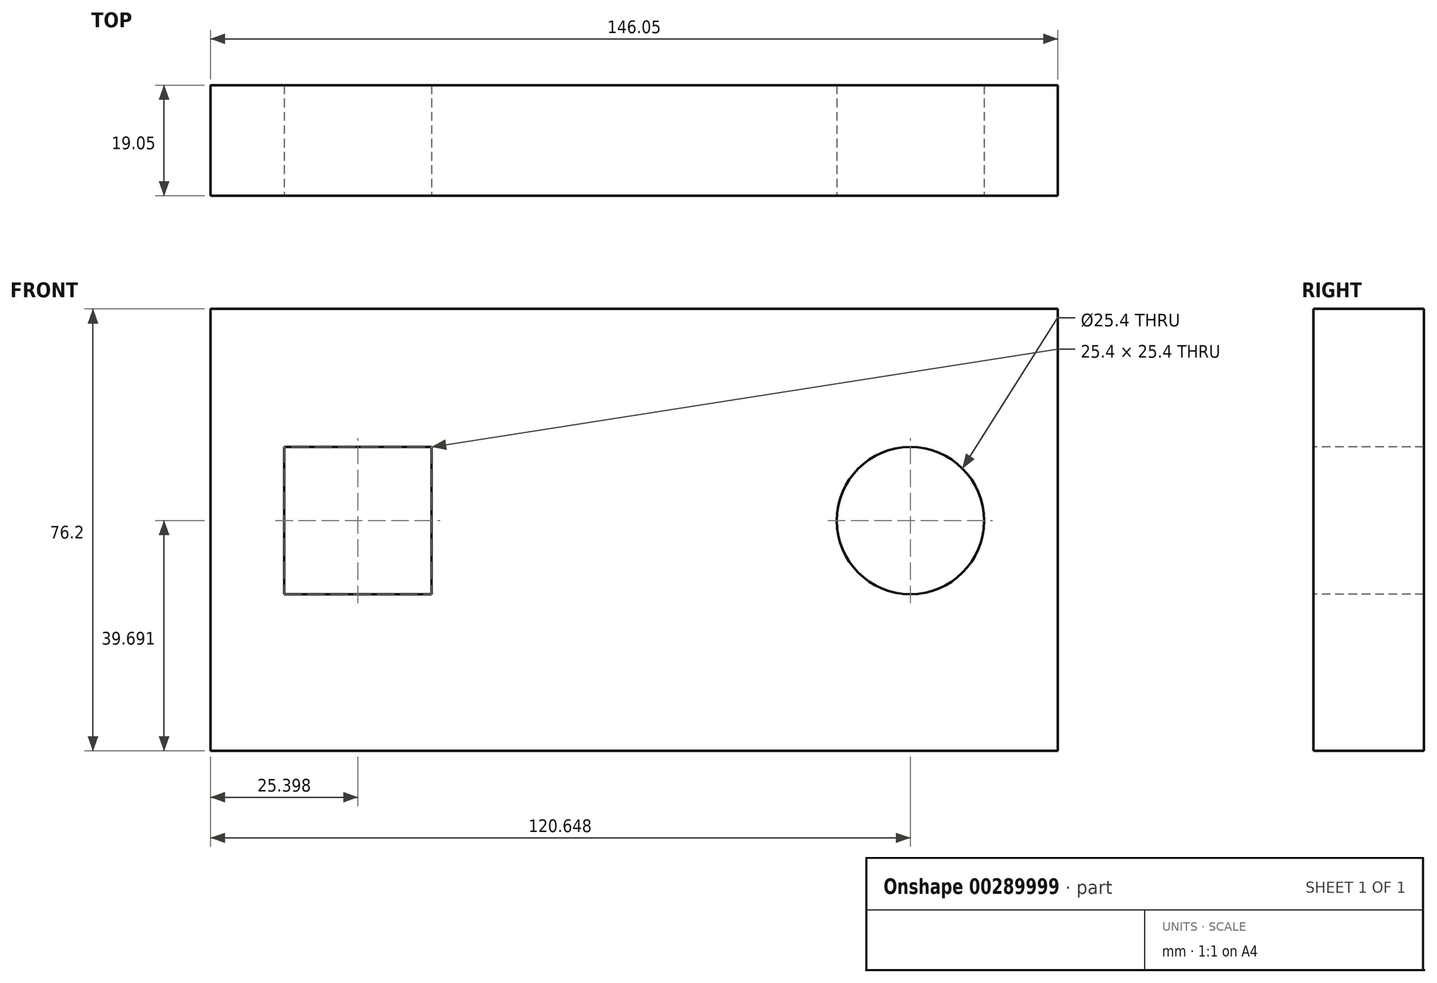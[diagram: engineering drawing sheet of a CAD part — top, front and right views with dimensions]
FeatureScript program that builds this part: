
annotation { "Feature Type Name" : "Feature", "Feature Type Description" : "" }
export const myFeature = defineFeature(function(context is Context, id is Id, definition is map)
    precondition{}
    {
        {
            var Q0;
            Q0=qCreatedBy(makeId("Front.planeOp"),FACE);
            var sketch = newSketch(context, id + "F0", { "sketchPlane" : qUnion([Q0])});
            skLineSegment(sketch, "E0.bottom", {"start": v(85.7, 16.61) * mm, "end": v(-60.34, 16.61) * mm});
            skLineSegment(sketch, "E0.top", {"start": v(85.7, 92.81) * mm, "end": v(-60.34, 92.81) * mm});
            skLineSegment(sketch, "E0.left", {"start": v(85.7, 16.61) * mm, "end": v(85.7, 92.81) * mm});
            skLineSegment(sketch, "E0.right", {"start": v(-60.34, 16.61) * mm, "end": v(-60.34, 92.81) * mm});
            skSolve(sketch);
        }
        {
            var Q0;
            Q0=makeQuery(id+"F0.imprint","IMPRINT",FACE,{"disambiguationData":[TD([[makeQuery(id+"F0.imprint","IMPRINT",EDGE,{"derivedFrom":sQuery(id+"F0.wireOp",EDGE,"E0.bottom")}),-1.0]])]});
            var sketch = newSketch(context, id + "F1", { "sketchPlane" : qUnion([Q0])});
            skLineSegment(sketch, "E1.bottom", {"start": v(-22.24, 43.6) * mm, "end": v(-47.64, 43.6) * mm});
            skLineSegment(sketch, "E1.top", {"start": v(-22.24, 69) * mm, "end": v(-47.64, 69) * mm});
            skLineSegment(sketch, "E1.left", {"start": v(-22.24, 43.6) * mm, "end": v(-22.24, 69) * mm});
            skLineSegment(sketch, "E1.right", {"start": v(-47.64, 43.6) * mm, "end": v(-47.64, 69) * mm});
            skPoint(sketch, "E1.middle", {"position": v(-34.94, 56.3) * mm});
            skSolve(sketch);
        }
        {
            var Q0;
            Q0=makeQuery(id+"F0.imprint","IMPRINT",FACE,{"disambiguationData":[TD([[makeQuery(id+"F0.imprint","IMPRINT",EDGE,{"derivedFrom":sQuery(id+"F0.wireOp",EDGE,"E0.bottom")}),-1.0]])]});
            var sketch = newSketch(context, id + "F2", { "sketchPlane" : qUnion([Q0])});
            skCircle(sketch, "E2", {"center": v(60.3, 56.3) * mm, "radius": 12.7 * mm});
            skSolve(sketch);
        }
        {
            var Q0;
            Q0=makeQuery(id+"F0.imprint","IMPRINT",FACE,{"disambiguationData":[TD([[makeQuery(id+"F0.imprint","IMPRINT",EDGE,{"derivedFrom":sQuery(id+"F0.wireOp",EDGE,"E0.bottom")}),-1.0]])]});
            extrude(context, id + "F3", {"entities" : qUnion([Q0]), "depth" : 19.05 * mm});
        }
        {
            var Q0;
            Q0 = qSketchRegion(id + "F1", true);
            extrude(context, id + "F4", {"entities" : qUnion([Q0]), "operationType" : NewBodyOperationType.ADD, "depth" : 25.4 * mm});
        }
        {
            var Q0;
            Q0=makeQuery(id+"F4.opExtrude","CAP_FACE",FACE,{"disambiguationData":[OSD([sQuery(id+"F1.wireOp",EDGE,"E1.bottom"),sQuery(id+"F1.wireOp",EDGE,"E1.top"),sQuery(id+"F1.wireOp",EDGE,"E1.left"),sQuery(id+"F1.wireOp",EDGE,"E1.right")])],"isStart":false});
            extrude(context, id + "F5", {"entities" : qUnion([Q0]), "operationType" : NewBodyOperationType.REMOVE, "oppositeDirection" : true, "depth" : 38.1 * mm});
        }
        {
            var Q0;
            Q0 = qSketchRegion(id + "F2", true);
            extrude(context, id + "F6", {"entities" : qUnion([Q0]), "operationType" : NewBodyOperationType.ADD, "depth" : 25.4 * mm});
        }
        {
            var Q0;
            Q0=makeQuery(id+"F6.opExtrude","CAP_FACE",FACE,{"disambiguationData":[OSD([sQuery(id+"F2.wireOp",EDGE,"E2")])],"isStart":false});
            extrude(context, id + "F7", {"entities" : qUnion([Q0]), "operationType" : NewBodyOperationType.REMOVE, "oppositeDirection" : true, "depth" : 25.4 * mm});
        }
    });
